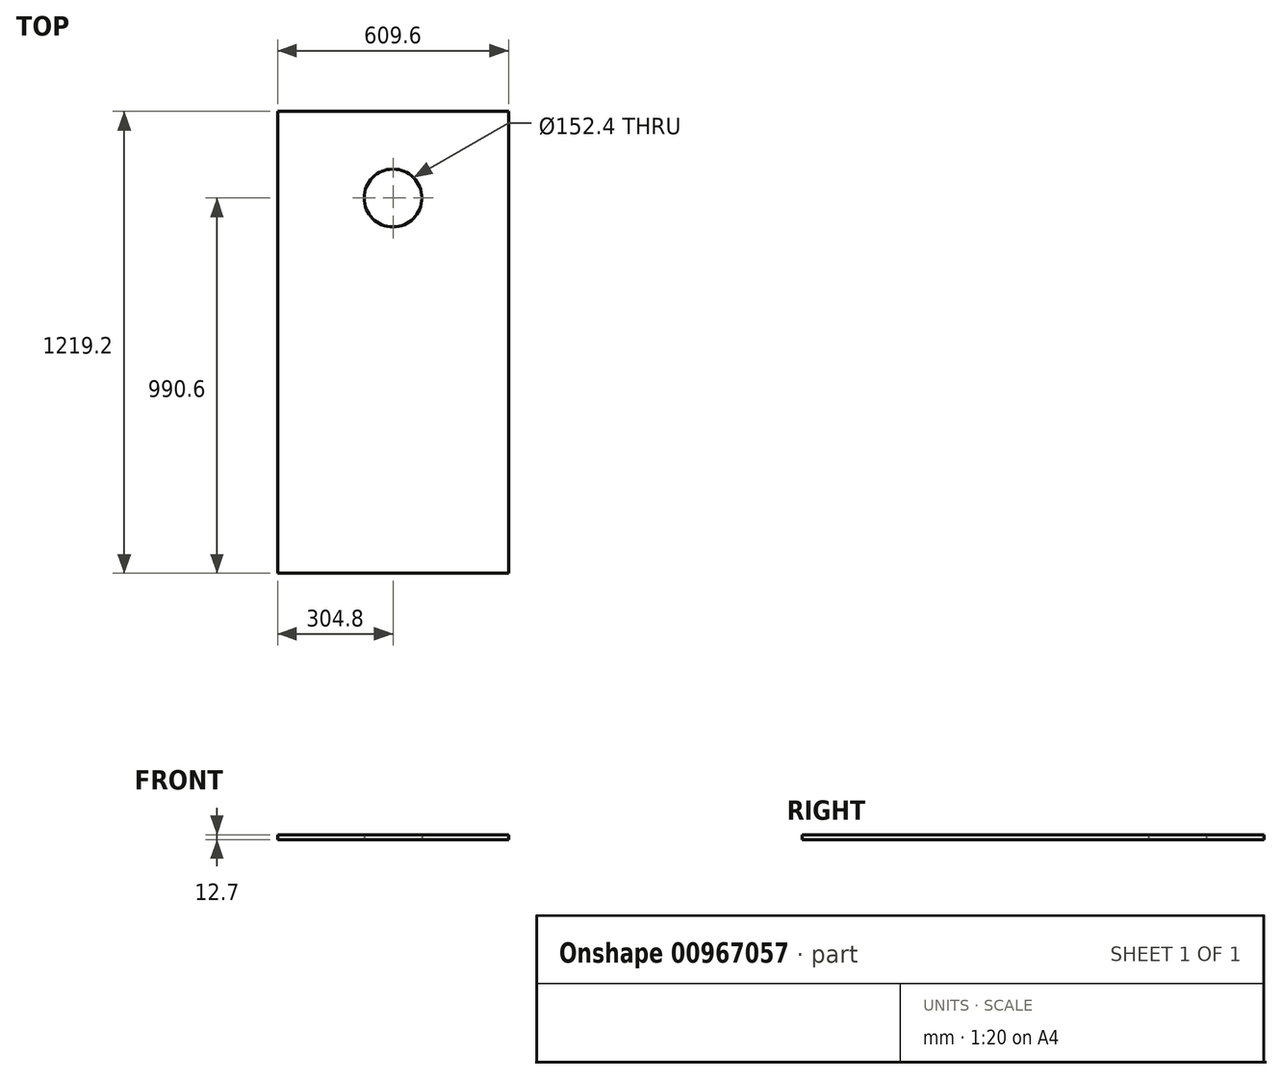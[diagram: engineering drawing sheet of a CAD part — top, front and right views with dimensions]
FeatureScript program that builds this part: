
annotation { "Feature Type Name" : "Feature", "Feature Type Description" : "" }
export const myFeature = defineFeature(function(context is Context, id is Id, definition is map)
    precondition{}
    {
        {
            var Q0;
            Q0=qCreatedBy(makeId("Top.planeOp"),FACE);
            var sketch = newSketch(context, id + "F0", { "sketchPlane" : qUnion([Q0])});
            skLineSegment(sketch, "E0.bottom", {"start": v(304.8, 609.6) * mm, "end": v(-304.8, 609.6) * mm});
            skLineSegment(sketch, "E0.top", {"start": v(304.8, -609.6) * mm, "end": v(-304.8, -609.6) * mm});
            skLineSegment(sketch, "E0.left", {"start": v(304.8, 609.6) * mm, "end": v(304.8, -609.6) * mm});
            skLineSegment(sketch, "E0.right", {"start": v(-304.8, 609.6) * mm, "end": v(-304.8, -609.6) * mm});
            skPoint(sketch, "E0.middle", {"position": v(0, 0) * mm});
            skCircle(sketch, "E1", {"center": v(0, 381) * mm, "radius": 76.2 * mm});
            skSolve(sketch);
        }
        {
            var Q0;
            Q0 = qSketchRegion(id + "F0", true);
            extrude(context, id + "F1", {"entities" : qUnion([Q0]), "depth" : 12.7 * mm, "offsetDistance" : 25.4 * mm});
        }
    });
